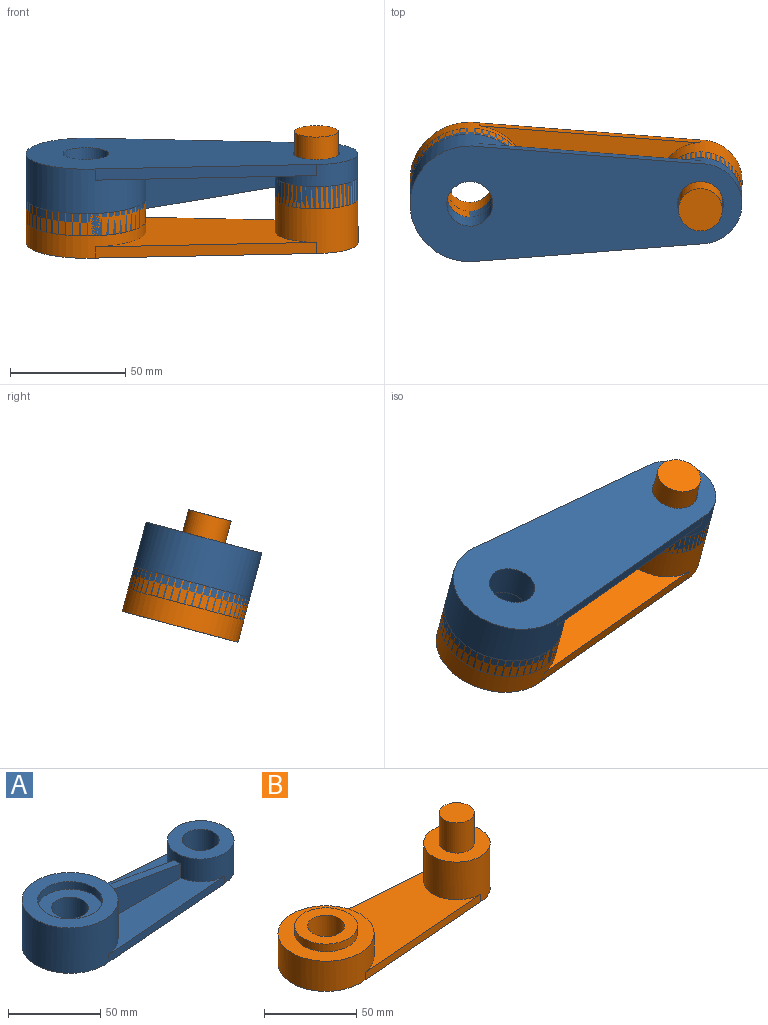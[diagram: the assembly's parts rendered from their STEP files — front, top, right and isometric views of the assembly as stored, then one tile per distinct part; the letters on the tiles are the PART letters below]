
ASSEMBLY  parts=2 mates=1
PART A: 18 faces, bbox 144.3x52.3x30.3 mm
  f0: plane 95.87x23.17mm, normal (0,0,1), area 1274.6mm2, adj f1,f5,f7,f11
  f1: cylinder r=26mm len=52mm, axis (0,0,-1), area 4440.4mm2, adj f0,f2,f3,f4,f5,f6,f9,f10
  f2: plane 52x52mm, normal (0,0,1), area 1161.6mm2, adj f1,f14
  f3: plane 144x52mm, normal (0,0,-1), area 5342.9mm2, adj f1,f4,f5,f7,f16,f17
  f4: plane 95.87x7.67mm, normal (0.08,-1,0), area 480.9mm2, adj f1,f3,f6,f7
  f5: plane 95.87x7.67mm, normal (0.08,1,0), area 480.9mm2, adj f0,f1,f3,f7
  f6: plane 95.87x23.17mm, normal (0,0,1), area 1274.6mm2, adj f1,f4,f7,f9
  f7: cylinder r=18mm len=36mm, axis (0,0,-1), area 1932.7mm2, adj f0,f3,f4,f5,f6,f8,f9,f11
  f8: plane 36x36mm, normal (0,0,1), area 703.7mm2, adj f7,f16
  f9: plane 56.3x19mm, normal (0,-1,0), area 796.3mm2, adj f1,f6,f7,f10,f13
  f10: plane 2.53x0.97mm, normal (-0.99,0,0.17), area 0.6mm2, adj f1,f9,f13
  f11: plane 56.3x19mm, normal (0,1,0), area 796.3mm2, adj f0,f1,f7,f12,f13
  f12: plane 2.53x0.97mm, normal (-0.99,0,0.17), area 0.6mm2, adj f1,f11,f13
  f13: plane 56.24x9.79mm, normal (0.17,0,0.99), area 284.5mm2, adj f1,f7,f9,f10,f11,f12
  f14: cylinder r=17.5mm len=35mm, axis (0,0,1), area 549.8mm2, adj f2,f15
  f15: plane 35x35mm, normal (0,0,1), area 648mm2, adj f14,f17
  f16: cylinder r=10mm len=20mm, axis (0,0,1), area 1256.6mm2, adj f3,f8
  f17: cylinder r=10mm len=25mm, axis (0,0,1), area 1570.8mm2, adj f3,f15
PART B: 13 faces, bbox 144x52x50 mm
  f0: cylinder r=26mm len=52mm, axis (0,0,-1), area 2900.4mm2, adj f1,f2,f3,f4,f5
  f1: plane 52x52mm, normal (0,0,1), area 1215.8mm2, adj f0,f8
  f2: plane 144x52mm, normal (0,0,-1), area 5657.1mm2, adj f0,f3,f4,f6,f12
  f3: plane 95.87x7.67mm, normal (0.08,-1,0), area 480.9mm2, adj f0,f2,f5,f6
  f4: plane 95.87x7.67mm, normal (0.08,1,0), area 480.9mm2, adj f0,f2,f5,f6
  f5: plane 95.87x51.34mm, normal (0,0,1), area 2829.7mm2, adj f0,f3,f4,f6
  f6: cylinder r=18mm len=36mm, axis (0,0,-1), area 3110.2mm2, adj f2,f3,f4,f5,f7
  f7: plane 36x36mm, normal (0,0,1), area 734.3mm2, adj f6,f10
  f8: cylinder r=17mm len=34mm, axis (0,0,-1), area 534.1mm2, adj f1,f9
  f9: plane 34x34mm, normal (0,0,1), area 593.8mm2, adj f8,f12
  f10: cylinder r=9.5mm len=20mm, axis (0,0,-1), area 1193.8mm2, adj f7,f11
  f11: plane 19x19mm, normal (0,0,1), area 283.5mm2, adj f10
  f12: cylinder r=10mm len=25mm, axis (0,0,1), area 1570.8mm2, adj f2,f9
PLACE A rot(axis=(-1,0,0),165deg) t=(-126.13,7.6,55.16)mm
PLACE B rot(axis=(1,0,0),15deg) t=(-126.13,17.95,16.52)mm
MATE fastened B.f10 <-> A.f7  axis (0,0.26,-0.97) through (-26.13,7.6,55.16)mm
